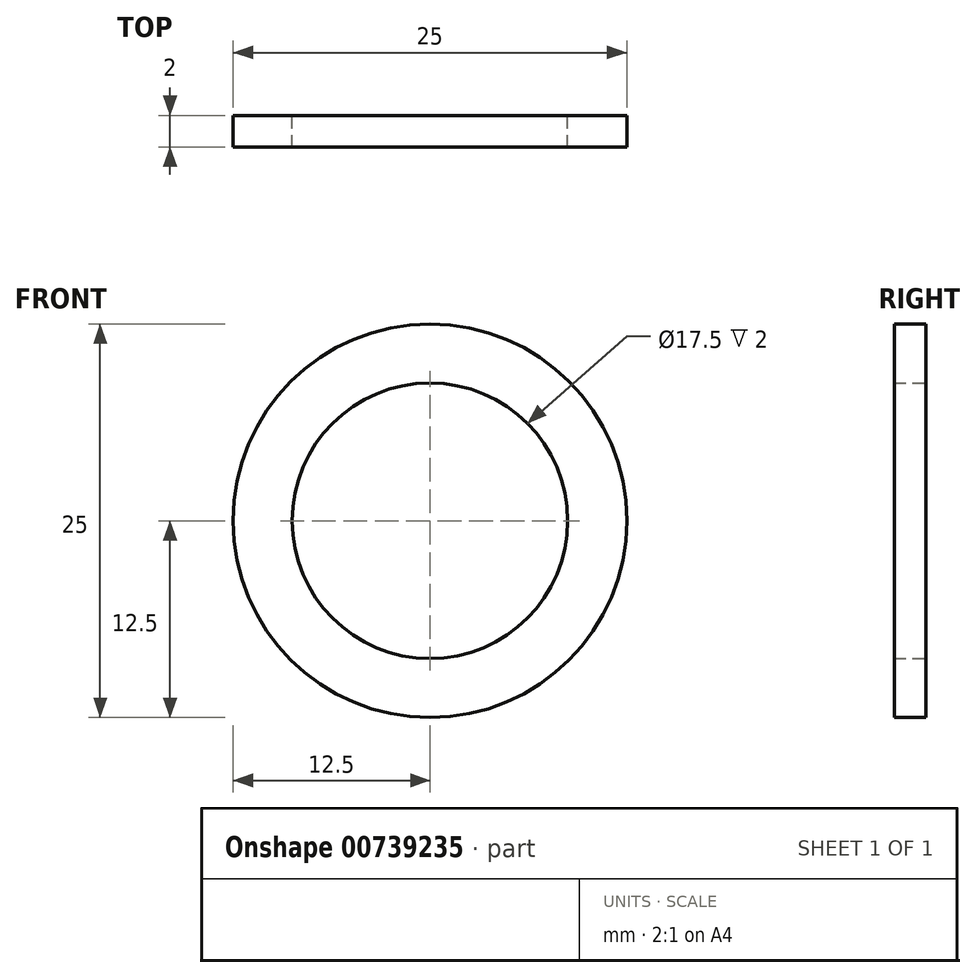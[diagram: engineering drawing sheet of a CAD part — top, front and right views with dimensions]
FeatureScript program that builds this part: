
annotation { "Feature Type Name" : "Feature", "Feature Type Description" : "" }
export const myFeature = defineFeature(function(context is Context, id is Id, definition is map)
    precondition{}
    {
        {
            var Q0;
            Q0=qCreatedBy(makeId("Front.planeOp"),FACE);
            var sketch = newSketch(context, id + "F0", { "sketchPlane" : qUnion([Q0])});
            skCircle(sketch, "E0", {"center": v(0, 0) * mm, "radius": 12.5 * mm});
            skCircle(sketch, "E1", {"center": v(0, 0) * mm, "radius": 8.75 * mm});
            skSolve(sketch);
        }
        {
            var Q0;
            Q0 = qSketchRegion(id + "F0", true);
            extrude(context, id + "F1", {"entities" : qUnion([Q0]), "depth" : 2 * mm, "offsetDistance" : 25.4 * mm});
        }
    });
